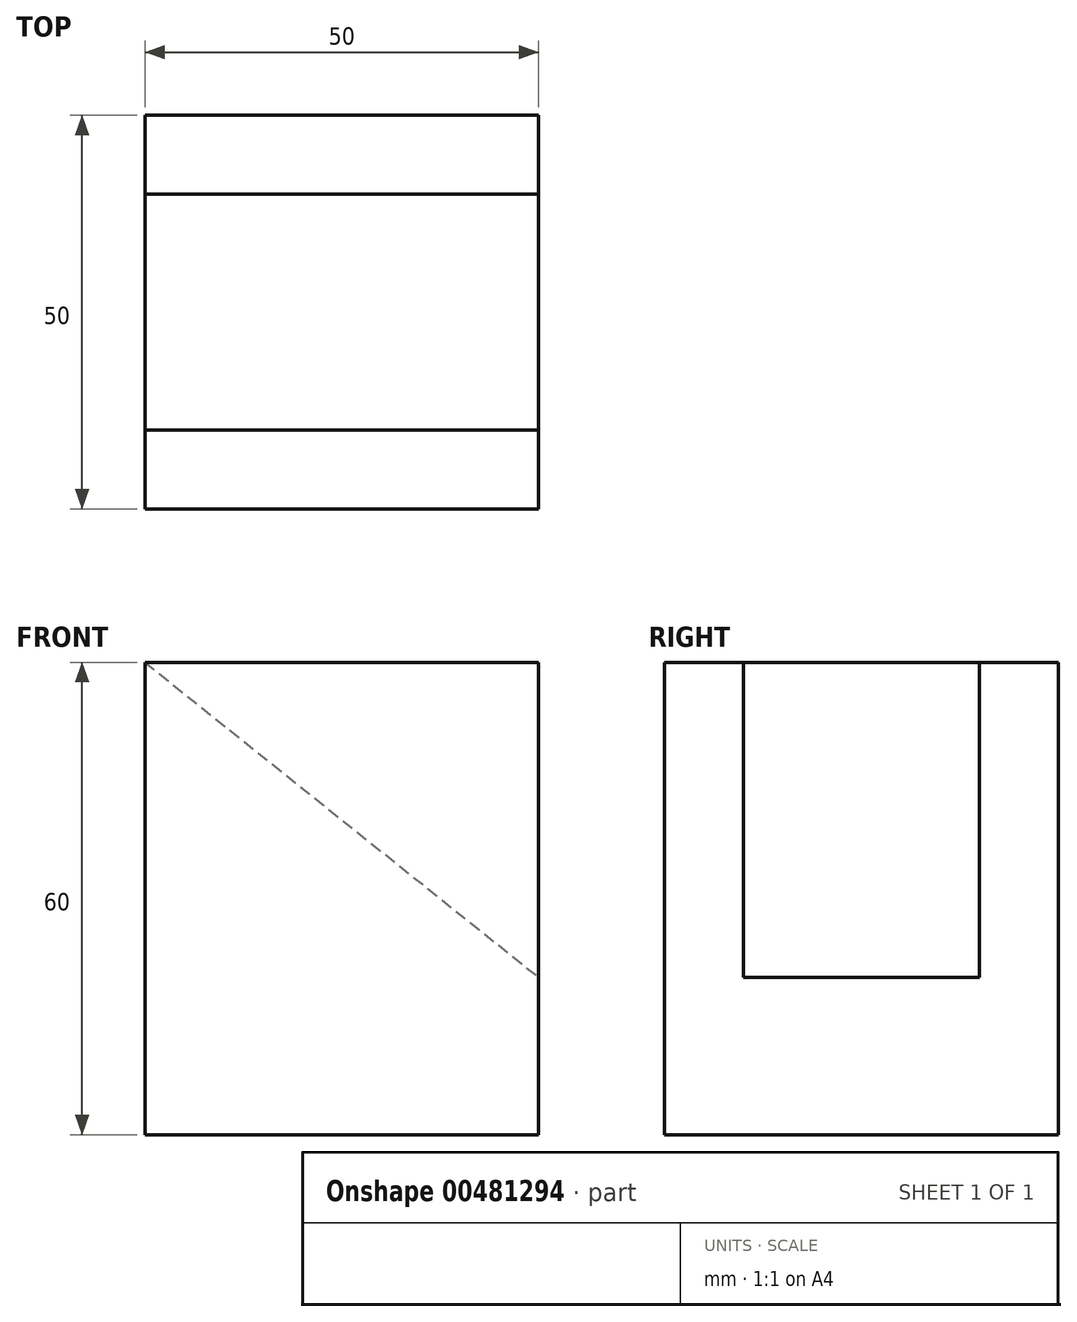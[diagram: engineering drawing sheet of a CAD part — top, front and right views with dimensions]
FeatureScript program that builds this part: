
annotation { "Feature Type Name" : "Feature", "Feature Type Description" : "" }
export const myFeature = defineFeature(function(context is Context, id is Id, definition is map)
    precondition{}
    {
        {
            var Q0;
            Q0=qCreatedBy(makeId("Right.planeOp"),FACE);
            var sketch = newSketch(context, id + "F0", { "sketchPlane" : qUnion([Q0])});
            skLineSegment(sketch, "E0", {"start": v(0, 0) * mm, "end": v(50, 0) * mm});
            skLineSegment(sketch, "E1", {"start": v(50, 0) * mm, "end": v(50, 60) * mm});
            skLineSegment(sketch, "E2", {"start": v(50, 60) * mm, "end": v(40, 60) * mm});
            skLineSegment(sketch, "E3", {"start": v(40, 60) * mm, "end": v(40, 20) * mm});
            skLineSegment(sketch, "E4", {"start": v(40, 20) * mm, "end": v(10, 20) * mm});
            skLineSegment(sketch, "E5", {"start": v(10, 20) * mm, "end": v(10, 60) * mm});
            skLineSegment(sketch, "E6", {"start": v(10, 60) * mm, "end": v(0, 60) * mm});
            skLineSegment(sketch, "E7", {"start": v(0, 60) * mm, "end": v(0, 0) * mm});
            skSolve(sketch);
        }
        {
            var Q0;
            Q0 = qSketchRegion(id + "F0", true);
            extrude(context, id + "F1", {"entities" : qUnion([Q0]), "depth" : 50 * mm});
        }
        {
            var Q0;
            Q0=makeQuery(id+"F1.opExtrude","SWEPT_FACE",FACE,{"disambiguationData":[OSD([sQuery(id+"F0.wireOp",EDGE,"E3")])]});
            var sketch = newSketch(context, id + "F2", { "sketchPlane" : qUnion([Q0])});
            skLineSegment(sketch, "E8", {"start": v(0, 60) * mm, "end": v(50, 20) * mm});
            skLineSegment(sketch, "E9", {"start": v(50, 20) * mm, "end": v(0, 20) * mm});
            skLineSegment(sketch, "E10", {"start": v(0, 20) * mm, "end": v(0, 60) * mm});
            skSolve(sketch);
        }
        {
            var Q0;
            Q0 = qSketchRegion(id + "F2", true);
            extrude(context, id + "F3", {"entities" : qUnion([Q0]), "operationType" : NewBodyOperationType.ADD, "depth" : 40 * mm});
        }
    });
